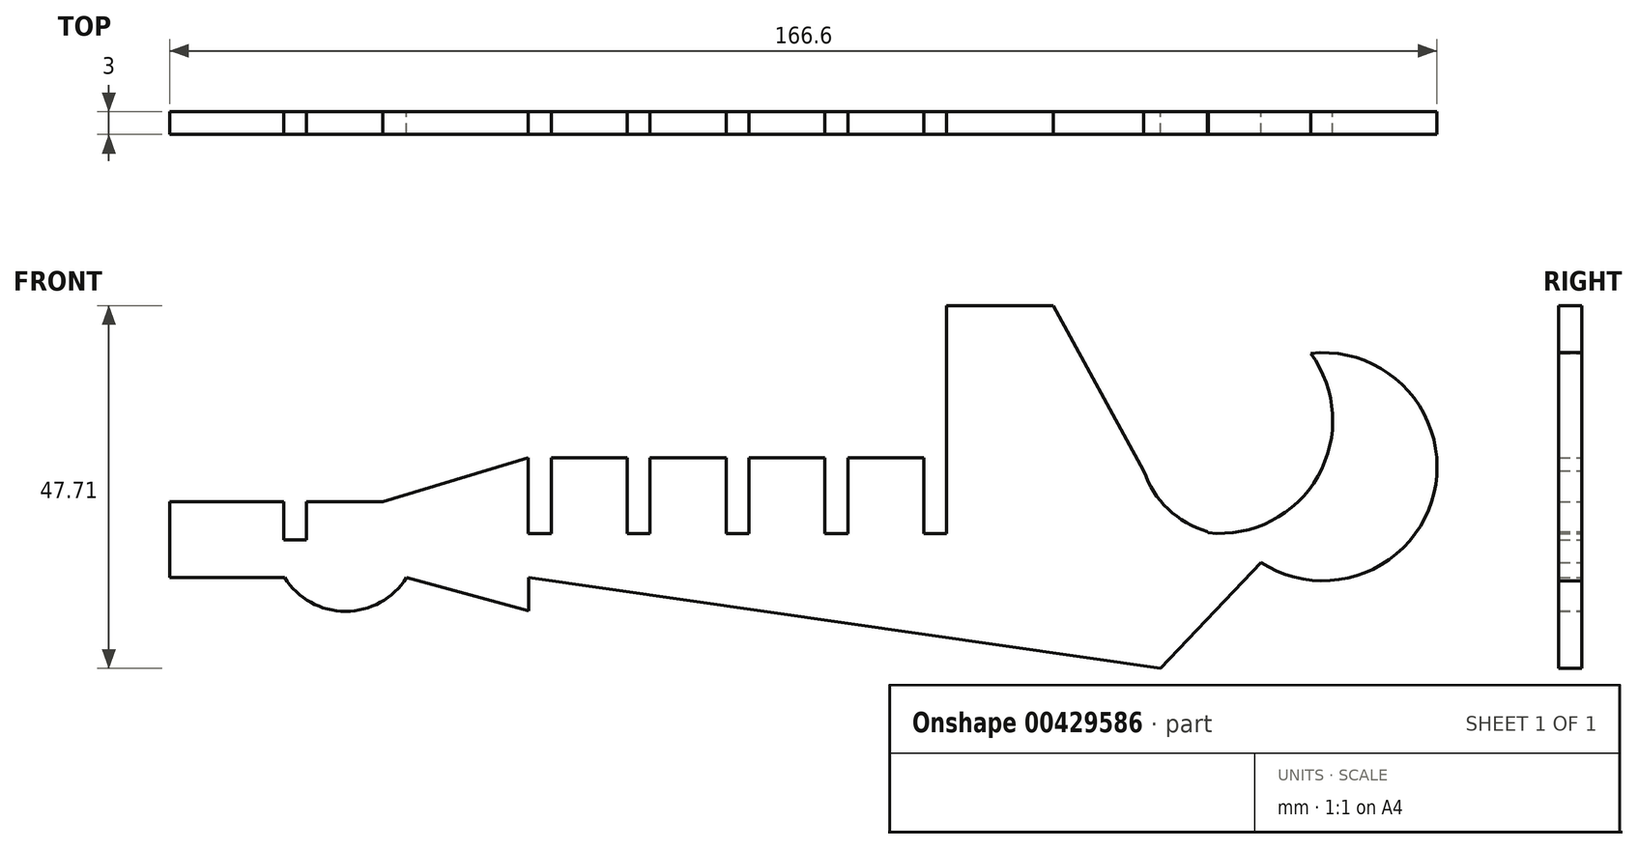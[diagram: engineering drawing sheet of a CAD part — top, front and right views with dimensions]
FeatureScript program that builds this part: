
annotation { "Feature Type Name" : "Feature", "Feature Type Description" : "" }
export const myFeature = defineFeature(function(context is Context, id is Id, definition is map)
    precondition{}
    {
        {
            var Q0;
            Q0=qCreatedBy(makeId("Front.planeOp"),FACE);
            var sketch = newSketch(context, id + "F0", { "sketchPlane" : qUnion([Q0])});
            skLineSegment(sketch, "E0", {"start": v(-51.79, 10) * mm, "end": v(-51.79, 0) * mm});
            skLineSegment(sketch, "E1.bottom", {"start": v(-51.79, 10) * mm, "end": v(-36.79, 10) * mm});
            skLineSegment(sketch, "E1.top", {"start": v(-51.79, 0) * mm, "end": v(-36.79, 0) * mm});
            skLineSegment(sketch, "E2.top", {"start": v(-36.79, 5) * mm, "end": v(-33.79, 5) * mm});
            skLineSegment(sketch, "E2.left", {"start": v(-36.79, 10) * mm, "end": v(-36.79, 5) * mm});
            skLineSegment(sketch, "E2.right", {"start": v(-33.79, 10) * mm, "end": v(-33.79, 5) * mm});
            skArc(sketch, "E3", {"start": v(-36.67, 0) * mm, "mid": v(-28.67, -4.43) * mm, "end": v(-20.67, 0) * mm});
            skLineSegment(sketch, "E4", {"start": v(-36.79, 0) * mm, "end": v(-36.67, 0) * mm});
            skLineSegment(sketch, "E5", {"start": v(-33.79, 10) * mm, "end": v(-23.79, 10) * mm});
            skLineSegment(sketch, "E6", {"start": v(-23.79, 10) * mm, "end": v(-4.64, 15.79) * mm});
            skLineSegment(sketch, "E7", {"start": v(-4.64, 15.79) * mm, "end": v(-4.64, 5.79) * mm});
            skLineSegment(sketch, "E8", {"start": v(-4.64, 5.79) * mm, "end": v(-1.64, 5.79) * mm});
            skPoint(sketch, "E9.start.orphan", {"position": v(-1.99, 13.34) * mm});
            skLineSegment(sketch, "E10.right", {"start": v(-1.64, 15.79) * mm, "end": v(-1.64, 5.79) * mm});
            skLineSegment(sketch, "E11", {"start": v(-1.64, 15.79) * mm, "end": v(8.36, 15.79) * mm});
            skPoint(sketch, "E12.start.orphan", {"position": v(5.86, 5.79) * mm});
            skPoint(sketch, "E13.start.orphan", {"position": v(9.75, 13.34) * mm});
            skPoint(sketch, "E14.start.orphan", {"position": v(15.8, 5.79) * mm});
            skPoint(sketch, "E15.start.orphan", {"position": v(21.36, 13.34) * mm});
            skPoint(sketch, "E16.start.orphan", {"position": v(26.5, 5.79) * mm});
            skPoint(sketch, "E17.start.orphan", {"position": v(32.6, 13.34) * mm});
            skPoint(sketch, "E18.start.orphan", {"position": v(39.4, 5.79) * mm});
            skLineSegment(sketch, "E19.top", {"start": v(8.36, 5.79) * mm, "end": v(11.36, 5.79) * mm});
            skLineSegment(sketch, "E19.left", {"start": v(8.36, 15.79) * mm, "end": v(8.36, 5.79) * mm});
            skLineSegment(sketch, "E19.right", {"start": v(11.36, 15.79) * mm, "end": v(11.36, 5.79) * mm});
            skLineSegment(sketch, "E20", {"start": v(11.36, 15.79) * mm, "end": v(21.36, 15.79) * mm});
            skLineSegment(sketch, "E21.top", {"start": v(21.36, 5.79) * mm, "end": v(24.36, 5.79) * mm});
            skLineSegment(sketch, "E21.left", {"start": v(21.36, 15.79) * mm, "end": v(21.36, 5.79) * mm});
            skLineSegment(sketch, "E21.right", {"start": v(24.36, 15.79) * mm, "end": v(24.36, 5.79) * mm});
            skLineSegment(sketch, "E22", {"start": v(24.36, 15.79) * mm, "end": v(34.36, 15.79) * mm});
            skLineSegment(sketch, "E23.top", {"start": v(34.36, 5.79) * mm, "end": v(37.36, 5.79) * mm});
            skLineSegment(sketch, "E23.left", {"start": v(34.36, 15.79) * mm, "end": v(34.36, 5.79) * mm});
            skLineSegment(sketch, "E23.right", {"start": v(37.36, 15.79) * mm, "end": v(37.36, 5.79) * mm});
            skLineSegment(sketch, "E24", {"start": v(37.36, 15.79) * mm, "end": v(47.36, 15.79) * mm});
            skLineSegment(sketch, "E25.top", {"start": v(47.34, 5.79) * mm, "end": v(50.34, 5.79) * mm});
            skLineSegment(sketch, "E25.left", {"start": v(47.34, 15.79) * mm, "end": v(47.34, 5.79) * mm});
            skLineSegment(sketch, "E25.right", {"start": v(50.34, 35.79) * mm, "end": v(50.34, 5.79) * mm});
            skLineSegment(sketch, "E26", {"start": v(50.34, 35.79) * mm, "end": v(64.34, 35.79) * mm});
            skLineSegment(sketch, "E27", {"start": v(64.34, 35.79) * mm, "end": v(77.8, 11.24) * mm});
            skArc(sketch, "E28", {"start": v(76.26, 14.06) * mm, "mid": v(79.84, 8.67) * mm, "end": v(85.65, 5.83) * mm});
            skPoint(sketch, "E29.end.orphan", {"position": v(99.8, 14.6) * mm});
            skArc(sketch, "E30", {"start": v(84.64, 6.07) * mm, "mid": v(84.7, 5.98) * mm, "end": v(84.74, 5.9) * mm});
            skArc(sketch, "E31", {"start": v(84.74, 5.9) * mm, "mid": v(99.14, 13.33) * mm, "end": v(98.2, 29.5) * mm});
            skArc(sketch, "E32", {"start": v(91.65, 2) * mm, "mid": v(114.4, 11.12) * mm, "end": v(98.2, 29.5) * mm});
            skLineSegment(sketch, "E33", {"start": v(-20.67, 0) * mm, "end": v(-4.6, -4.36) * mm});
            skLineSegment(sketch, "E34", {"start": v(-4.6, -4.36) * mm, "end": v(-4.6, 0) * mm});
            skLineSegment(sketch, "E35", {"start": v(-4.6, 0) * mm, "end": v(78.48, -11.92) * mm});
            skLineSegment(sketch, "E36", {"start": v(78.48, -11.92) * mm, "end": v(91.65, 2) * mm});
            skPoint(sketch, "E37.end.orphan", {"position": v(114.8, 14.6) * mm});
            skSolve(sketch);
        }
        {
            var Q0;
            Q0=makeQuery(id+"F0.imprint","IMPRINT",FACE,{"disambiguationData":[TD([[makeQuery(id+"F0.imprint","IMPRINT",EDGE,{"derivedFrom":sQuery(id+"F0.wireOp",EDGE,"E1.bottom")}),-1.0]])]});
            extrude(context, id + "F1", {"entities" : qUnion([Q0]), "depth" : 3 * mm});
        }
    });
